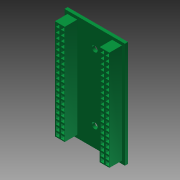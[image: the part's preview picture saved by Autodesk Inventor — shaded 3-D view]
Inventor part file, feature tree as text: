
AUTODESK INVENTOR PART (.ipt)
format: ipt  version: 2012 (Build 160160000, 160)  size: 448,512 bytes
history: native  units: in
note: dims shown in document units (in); Inventor stores cm internally (conversion verified against a paired STEP export)
features: extrude x2, sketch x1
ambient origin geometry x8: Origin, YZ Plane, XZ Plane, XY Plane, X Axis, Y Axis, Z Axis, Center Point
bodies: Solid1 (feature_tree)
feature tree (3):
  sketch  "Sketch1"  dims[d3=2.0069in d4=0.1969in d5=0.0591in d6=0.0591in d7=0.0669in d8=0.0669in d9=0.1in d10=0.0669in d11=0.0669in d12=0.0197in d13=0.0197in d14=0.0197in d15=0.0669in d16=0.0669in d17=0.1in d18=0.0669in d19=0.0669in d21=0.1in d22=0.1in d23=0.0197in d24=3.937in d26=0.2in d27=0.3937in d29=1.0in d31=0.7874in d33=0.9in d34=0.3937in d36=1.0in d38=0.0591in d39=0.0591in d40=0.6075in d41=0.6075in d42=0.3937in d43=0.3937in d44=0.1181in d45=0.1181in d46=0.063in d47=0.0in d48=0.315in d49=0.0in]
  extrude  "Extrusion1"  Depth=0.1969in
  extrude  "Extrusion2"  Depth=0.0591in
